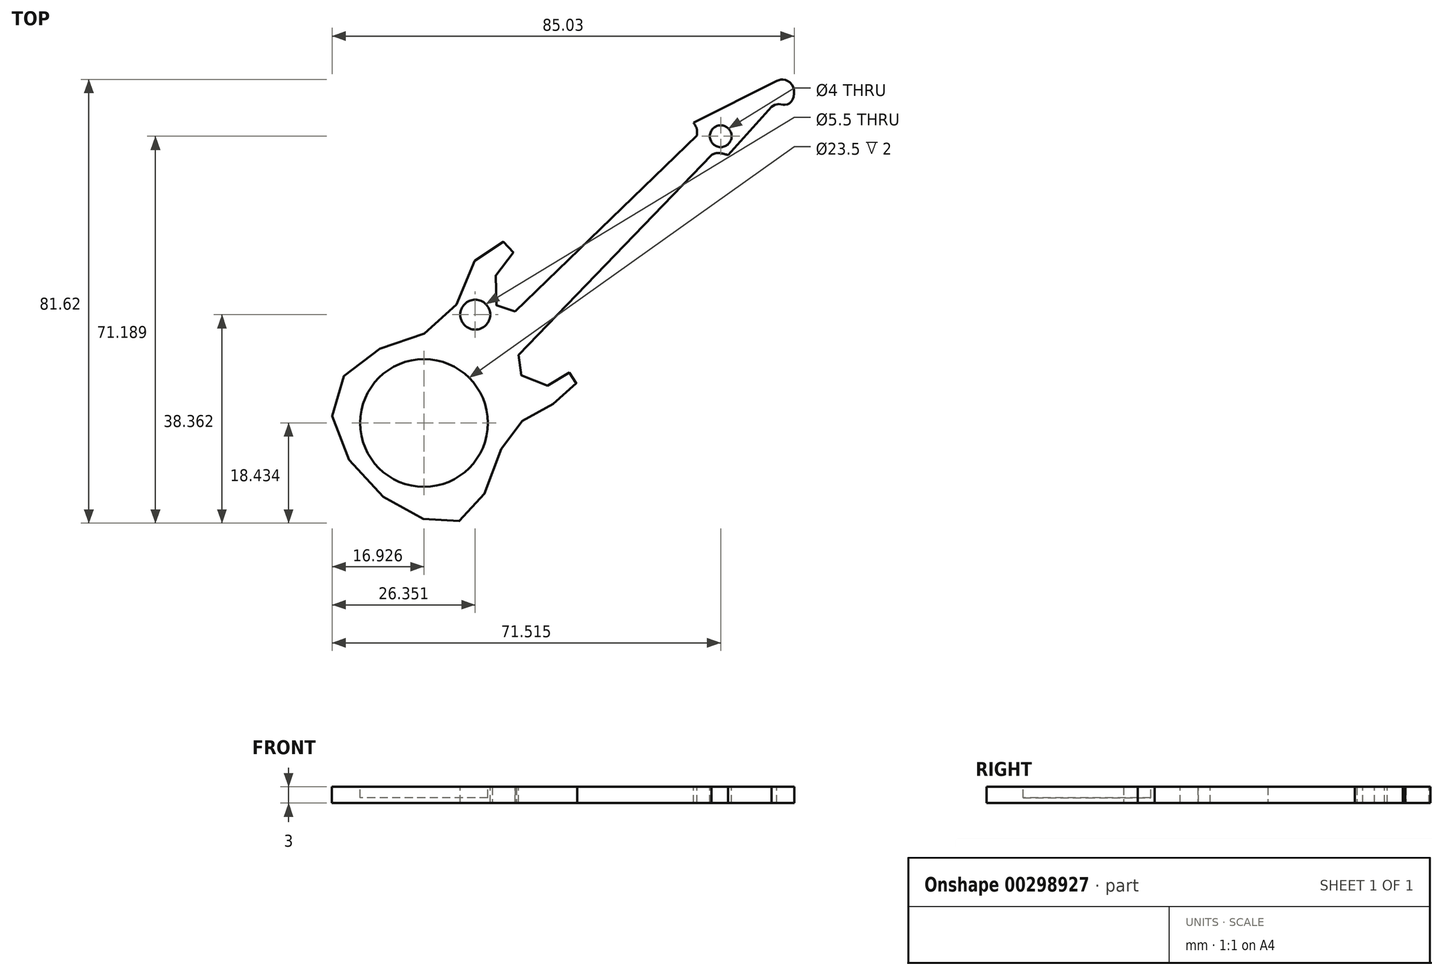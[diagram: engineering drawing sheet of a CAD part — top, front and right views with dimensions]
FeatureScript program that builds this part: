
annotation { "Feature Type Name" : "Feature", "Feature Type Description" : "" }
export const myFeature = defineFeature(function(context is Context, id is Id, definition is map)
    precondition{}
    {
        {
            var Q0;
            Q0=qCreatedBy(makeId("Top.planeOp"),FACE);
            var sketch = newSketch(context, id + "F0", { "sketchPlane" : qUnion([Q0])});
            skPoint(sketch, "E0.0.internal.orphan", {"position": v(0, 21.76) * mm});
            skPoint(sketch, "E1.0.internal.orphan", {"position": v(-2.06, 23.98) * mm});
            skPoint(sketch, "E1.2.internal.orphan", {"position": v(-2.06, 26.33) * mm});
            skPoint(sketch, "E2.16.internal.snap0", {"position": v(-9.17, -54.77) * mm});
            skFitSpline(sketch, "E2", {"points": [v(-18.6, -12.3) * mm, v(-21.41, -11.93) * mm, v(-22.54, -6.6) * mm, v(-18.98, -1.53) * mm, v(-18.88, 0) * mm, v(-24.32, -0.79) * mm, v(-31.06, -13.62) * mm, v(-44.27, -19.52) * mm, v(-52.23, -29.45) * mm, v(-46.05, -43.5) * mm, v(-33.55, -51.04) * mm, v(-25.95, -48.83) * mm, v(-20.11, -35.48) * mm, v(-14.27, -30.79) * mm, v(-7.55, -26.01) * mm, v(-7.55, -23.72) * mm, v(-9.17, -23.8) * mm, v(-13.4, -26.1) * mm, v(-18.08, -23.18) * mm, v(-17.99, -20.35) * mm], "startDerivative": vector(-90.73, -12.45) * mm, "endDerivative": vector(25.76, 81.55) * mm});
            skLineSegment(sketch, "E3", {"start": v(-18.6, -12.3) * mm, "end": v(14.83, 20.06) * mm});
            skLineSegment(sketch, "E4", {"start": v(-17.99, -20.35) * mm, "end": v(17.51, 16.44) * mm});
            skFitSpline(sketch, "E5", {"points": [v(14.83, 20.06) * mm, v(14.83, 21.18) * mm, v(14.23, 22.4) * mm], "startDerivative": vector(0.27, 2.35) * mm, "endDerivative": vector(-1.44, 2.32) * mm});
            skFitSpline(sketch, "E6", {"points": [v(17.51, 16.44) * mm, v(18.64, 16.82) * mm, v(20.56, 16.44) * mm], "startDerivative": vector(2.38, 1.2) * mm, "endDerivative": vector(3.65, -1.11) * mm});
            skLineSegment(sketch, "E7", {"start": v(14.23, 22.4) * mm, "end": v(29.55, 30.08) * mm});
            skLineSegment(sketch, "E8", {"start": v(20.56, 16.44) * mm, "end": v(28.57, 25.3) * mm});
            skFitSpline(sketch, "E9", {"points": [v(28.57, 25.3) * mm, v(29.7, 25.81) * mm, v(30.91, 25.72) * mm, v(32.32, 26.38) * mm, v(32.5, 29.06) * mm, v(30.85, 30.33) * mm, v(29.55, 30.08) * mm], "startDerivative": vector(7.69, 4.86) * mm, "endDerivative": vector(-8.22, -3.2) * mm});
            skCircle(sketch, "E10", {"center": v(19.22, 19.9) * mm, "radius": 2 * mm});
            skCircle(sketch, "E11", {"center": v(-25.94, -12.92) * mm, "radius": 2.75 * mm});
            skSolve(sketch);
        }
        {
            var Q0;
            Q0 = qSketchRegion(id + "F0", true);
            extrude(context, id + "F1", {"entities" : qUnion([Q0]), "oppositeDirection" : true, "depth" : 3 * mm});
        }
        {
            var Q0;
            Q0=makeQuery(id+"F1.opExtrude","CAP_FACE",FACE,{"disambiguationData":[OSD([sQuery(id+"F0.wireOp",EDGE,"E2"),sQuery(id+"F0.wireOp",EDGE,"E3"),sQuery(id+"F0.wireOp",EDGE,"E4"),sQuery(id+"F0.wireOp",EDGE,"E5"),sQuery(id+"F0.wireOp",EDGE,"E6"),sQuery(id+"F0.wireOp",EDGE,"E7"),sQuery(id+"F0.wireOp",EDGE,"E8"),sQuery(id+"F0.wireOp",EDGE,"E9"),sQuery(id+"F0.wireOp",EDGE,"E10"),sQuery(id+"F0.wireOp",EDGE,"E11")])],"isStart":true});
            var sketch = newSketch(context, id + "F2", { "sketchPlane" : qUnion([Q0])});
            skCircle(sketch, "E12", {"center": v(-35.36, -32.85) * mm, "radius": 11.75 * mm});
            skSolve(sketch);
        }
        {
            var Q0;
            Q0 = qSketchRegion(id + "F2", true);
            extrude(context, id + "F3", {"entities" : qUnion([Q0]), "operationType" : NewBodyOperationType.REMOVE, "oppositeDirection" : true, "depth" : 2 * mm});
        }
    });
